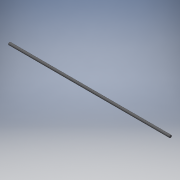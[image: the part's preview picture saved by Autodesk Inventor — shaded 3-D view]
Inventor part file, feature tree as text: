
AUTODESK INVENTOR PART (.ipt)
format: ipt  version: 2016 (Build 200138000, 138)  size: 122,880 bytes
history: native  units: mm
features: other x7, revolve x3, sketch x3, thread x1
ambient origin geometry x8: Origin, YZ Plane, XZ Plane, XY Plane, X Axis, Y Axis, Z Axis, Center Point
bodies: Solid1 (feature_tree)
feature tree (14):
  revolve  "Revolution1"  [1 undecoded]
  thread  "Thread1"  [1 undecoded]
  revolve  "Revolution2"  [1 undecoded]
  revolve  "Revolution3"  [1 undecoded]
  other  "bnt_s_1_XY"
  other  "bnt_s_1_YZ"
  other  "bnt_s_1_ZX"
  other  "bnt_s_1_X"
  other  "bnt_s_1_Y"
  other  "bnt_s_1_Z"
  other  "bnt_s_1_Center"
  sketch  "Sketch_1"  dims[d0=360.0deg d1=1258.0mm d2=0.0mm d3=360.0deg]
  sketch  "Sketch_2"  dims[d4=360.0deg d5=0.0mm]
  sketch  "Sketch_3"
note: 4 required parameter values undecoded (feature->parameter linkage not recoverable at this tier; creation-order binding heuristic only, values carry confidence <= 0.55)